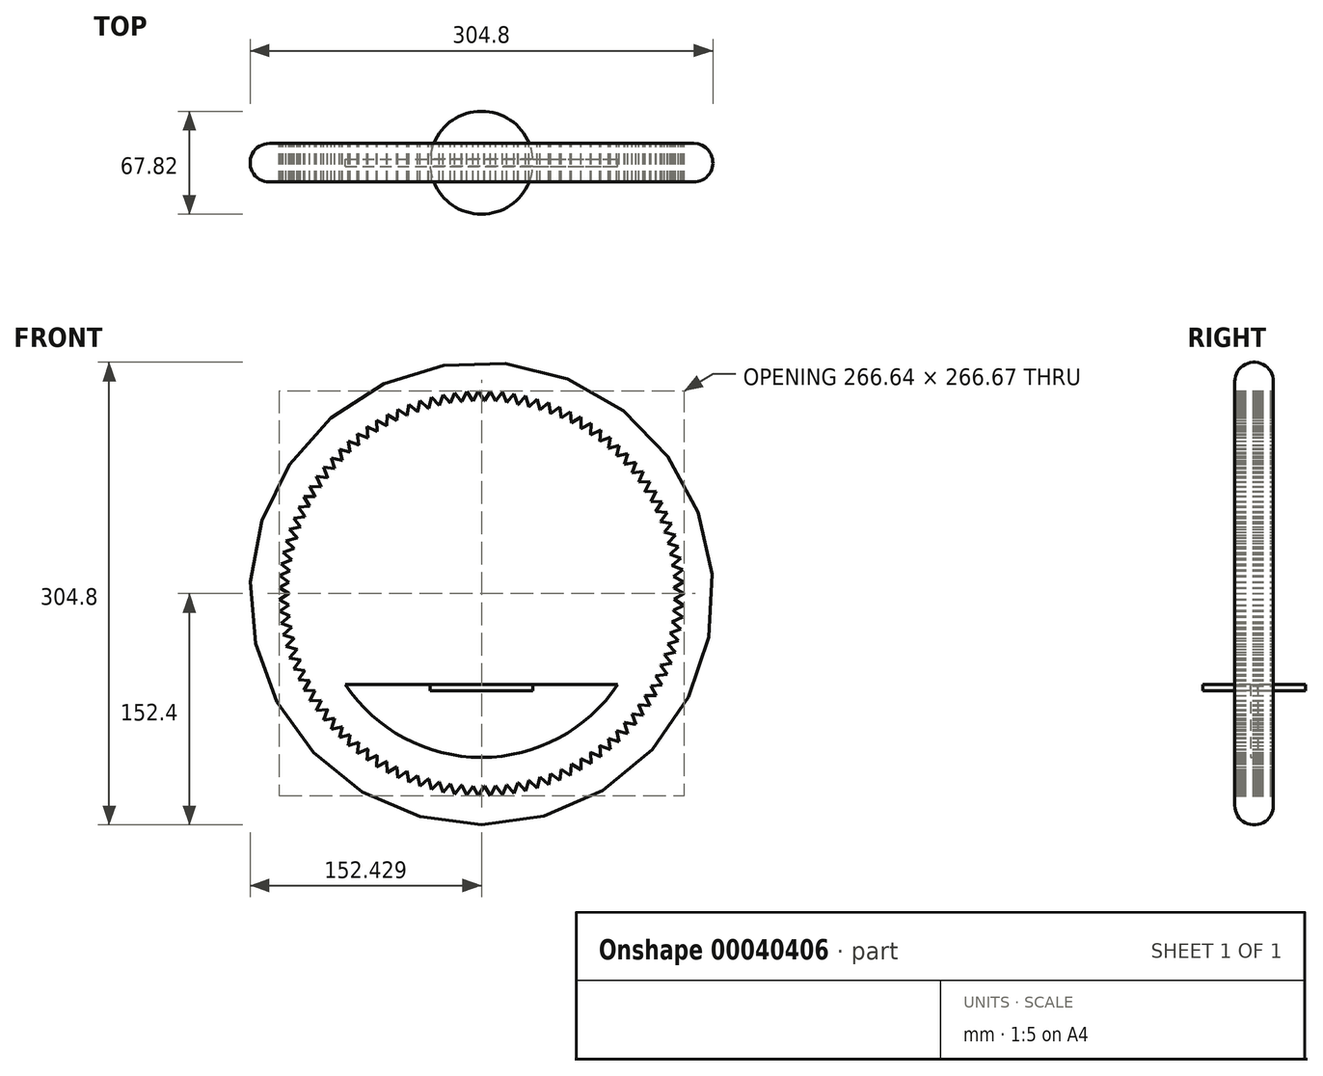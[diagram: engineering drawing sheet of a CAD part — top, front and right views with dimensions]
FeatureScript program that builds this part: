
annotation { "Feature Type Name" : "Feature", "Feature Type Description" : "" }
export const myFeature = defineFeature(function(context is Context, id is Id, definition is map)
    precondition{}
    {
        {
            var Q0;
            Q0=qCreatedBy(makeId("Front.planeOp"),FACE);
            var sketch = newSketch(context, id + "F0", { "sketchPlane" : qUnion([Q0])});
            skCircle(sketch, "E0", {"center": v(0, 0) * mm, "radius": 152.4 * mm});
            skCircle(sketch, "E1", {"center": v(0, 0) * mm, "radius": 127 * mm});
            skCircle(sketch, "E2", {"center": v(0, 0) * mm, "radius": 133.35 * mm, "construction": true});
            skLineSegment(sketch, "E3", {"start": v(133.35, 0) * mm, "end": v(126.95, 3.7) * mm});
            skLineSegment(sketch, "E4", {"start": v(133.35, 0) * mm, "end": v(126.95, -3.7) * mm});
            skLineSegment(sketch, "E5", {"start": v(0, 0) * mm, "end": v(133.35, 0) * mm, "construction": true});
            skLineSegment(sketch, "E6.1.0", {"start": v(133.12, 7.83) * mm, "end": v(126.94, 3.76) * mm});
            skLineSegment(sketch, "E6.1.1", {"start": v(133.12, 7.83) * mm, "end": v(126.51, 11.14) * mm});
            skLineSegment(sketch, "E6.2.0", {"start": v(132.43, 15.63) * mm, "end": v(126.5, 11.2) * mm});
            skLineSegment(sketch, "E6.2.1", {"start": v(132.43, 15.63) * mm, "end": v(125.64, 18.55) * mm});
            skLineSegment(sketch, "E6.3.0", {"start": v(131.29, 23.37) * mm, "end": v(125.63, 18.6) * mm});
            skLineSegment(sketch, "E6.3.1", {"start": v(131.29, 23.37) * mm, "end": v(124.33, 25.89) * mm});
            skLineSegment(sketch, "E6.4.0", {"start": v(129.69, 31.03) * mm, "end": v(124.32, 25.95) * mm});
            skLineSegment(sketch, "E6.4.1", {"start": v(129.69, 31.03) * mm, "end": v(122.6, 33.14) * mm});
            skLineSegment(sketch, "E6.5.0", {"start": v(127.64, 38.6) * mm, "end": v(122.58, 33.2) * mm});
            skLineSegment(sketch, "E6.5.1", {"start": v(127.64, 38.6) * mm, "end": v(120.44, 40.28) * mm});
            skLineSegment(sketch, "E6.6.0", {"start": v(125.16, 46.02) * mm, "end": v(120.42, 40.34) * mm});
            skLineSegment(sketch, "E6.6.1", {"start": v(125.16, 46.02) * mm, "end": v(117.87, 47.28) * mm});
            skLineSegment(sketch, "E6.7.0", {"start": v(122.24, 53.28) * mm, "end": v(117.85, 47.33) * mm});
            skLineSegment(sketch, "E6.7.1", {"start": v(122.24, 53.28) * mm, "end": v(114.9, 54.11) * mm});
            skLineSegment(sketch, "E6.8.0", {"start": v(118.9, 60.37) * mm, "end": v(114.87, 54.17) * mm});
            skLineSegment(sketch, "E6.8.1", {"start": v(118.9, 60.37) * mm, "end": v(111.52, 60.76) * mm});
            skLineSegment(sketch, "E6.9.0", {"start": v(115.16, 67.24) * mm, "end": v(111.5, 60.82) * mm});
            skLineSegment(sketch, "E6.9.1", {"start": v(115.16, 67.24) * mm, "end": v(107.76, 67.2) * mm});
            skLineSegment(sketch, "E6.10.0", {"start": v(111.01, 73.88) * mm, "end": v(107.73, 67.26) * mm});
            skLineSegment(sketch, "E6.10.1", {"start": v(111.01, 73.88) * mm, "end": v(103.63, 73.41) * mm});
            skLineSegment(sketch, "E6.11.0", {"start": v(106.48, 80.27) * mm, "end": v(103.6, 73.46) * mm});
            skLineSegment(sketch, "E6.11.1", {"start": v(106.48, 80.27) * mm, "end": v(99.15, 79.37) * mm});
            skLineSegment(sketch, "E6.12.0", {"start": v(101.6, 86.38) * mm, "end": v(99.1, 79.42) * mm});
            skLineSegment(sketch, "E6.12.1", {"start": v(101.6, 86.38) * mm, "end": v(94.32, 85.05) * mm});
            skLineSegment(sketch, "E6.13.0", {"start": v(96.35, 92.2) * mm, "end": v(94.28, 85.1) * mm});
            skLineSegment(sketch, "E6.13.1", {"start": v(96.35, 92.2) * mm, "end": v(89.16, 90.44) * mm});
            skLineSegment(sketch, "E6.14.0", {"start": v(90.77, 97.69) * mm, "end": v(89.12, 90.48) * mm});
            skLineSegment(sketch, "E6.14.1", {"start": v(90.77, 97.69) * mm, "end": v(83.7, 95.51) * mm});
            skLineSegment(sketch, "E6.15.0", {"start": v(84.88, 102.85) * mm, "end": v(83.66, 95.56) * mm});
            skLineSegment(sketch, "E6.15.1", {"start": v(84.88, 102.85) * mm, "end": v(77.95, 100.26) * mm});
            skLineSegment(sketch, "E6.16.0", {"start": v(78.7, 107.65) * mm, "end": v(77.9, 100.3) * mm});
            skLineSegment(sketch, "E6.16.1", {"start": v(78.7, 107.65) * mm, "end": v(71.93, 104.66) * mm});
            skLineSegment(sketch, "E6.17.0", {"start": v(72.24, 112.08) * mm, "end": v(71.88, 104.7) * mm});
            skLineSegment(sketch, "E6.17.1", {"start": v(72.24, 112.08) * mm, "end": v(65.67, 108.7) * mm});
            skLineSegment(sketch, "E6.18.0", {"start": v(65.54, 116.13) * mm, "end": v(65.61, 108.74) * mm});
            skLineSegment(sketch, "E6.18.1", {"start": v(65.54, 116.13) * mm, "end": v(59.17, 112.37) * mm});
            skLineSegment(sketch, "E6.19.0", {"start": v(58.61, 119.78) * mm, "end": v(59.12, 112.4) * mm});
            skLineSegment(sketch, "E6.19.1", {"start": v(58.61, 119.78) * mm, "end": v(52.48, 115.65) * mm});
            skLineSegment(sketch, "E6.20.0", {"start": v(51.48, 123.01) * mm, "end": v(52.42, 115.68) * mm});
            skLineSegment(sketch, "E6.20.1", {"start": v(51.48, 123.01) * mm, "end": v(45.6, 118.53) * mm});
            skLineSegment(sketch, "E6.21.0", {"start": v(44.17, 125.82) * mm, "end": v(45.54, 118.55) * mm});
            skLineSegment(sketch, "E6.21.1", {"start": v(44.17, 125.82) * mm, "end": v(38.56, 121) * mm});
            skLineSegment(sketch, "E6.22.0", {"start": v(36.71, 128.2) * mm, "end": v(38.5, 121.02) * mm});
            skLineSegment(sketch, "E6.22.1", {"start": v(36.71, 128.2) * mm, "end": v(31.4, 123.06) * mm});
            skLineSegment(sketch, "E6.23.0", {"start": v(29.13, 130.13) * mm, "end": v(31.34, 123.07) * mm});
            skLineSegment(sketch, "E6.23.1", {"start": v(29.13, 130.13) * mm, "end": v(24.12, 124.69) * mm});
            skLineSegment(sketch, "E6.24.0", {"start": v(21.44, 131.62) * mm, "end": v(24.06, 124.7) * mm});
            skLineSegment(sketch, "E6.24.1", {"start": v(21.44, 131.62) * mm, "end": v(16.76, 125.89) * mm});
            skLineSegment(sketch, "E6.25.0", {"start": v(13.68, 132.65) * mm, "end": v(16.7, 125.9) * mm});
            skLineSegment(sketch, "E6.25.1", {"start": v(13.68, 132.65) * mm, "end": v(9.34, 126.66) * mm});
            skLineSegment(sketch, "E6.26.0", {"start": v(5.87, 133.22) * mm, "end": v(9.28, 126.66) * mm});
            skLineSegment(sketch, "E6.26.1", {"start": v(5.87, 133.22) * mm, "end": v(1.9, 126.99) * mm});
            skLineSegment(sketch, "E6.27.0", {"start": v(-1.96, 133.34) * mm, "end": v(1.83, 126.99) * mm});
            skLineSegment(sketch, "E6.27.1", {"start": v(-1.96, 133.34) * mm, "end": v(-5.56, 126.88) * mm});
            skLineSegment(sketch, "E6.28.0", {"start": v(-9.78, 133) * mm, "end": v(-5.62, 126.88) * mm});
            skLineSegment(sketch, "E6.28.1", {"start": v(-9.78, 133) * mm, "end": v(-13, 126.33) * mm});
            skLineSegment(sketch, "E6.29.0", {"start": v(-17.57, 132.19) * mm, "end": v(-13.06, 126.33) * mm});
            skLineSegment(sketch, "E6.29.1", {"start": v(-17.57, 132.19) * mm, "end": v(-20.39, 125.35) * mm});
            skLineSegment(sketch, "E6.30.0", {"start": v(-25.3, 130.93) * mm, "end": v(-20.45, 125.34) * mm});
            skLineSegment(sketch, "E6.30.1", {"start": v(-25.3, 130.93) * mm, "end": v(-27.71, 123.94) * mm});
            skLineSegment(sketch, "E6.31.0", {"start": v(-32.94, 129.22) * mm, "end": v(-27.77, 123.93) * mm});
            skLineSegment(sketch, "E6.31.1", {"start": v(-32.94, 129.22) * mm, "end": v(-34.94, 122.1) * mm});
            skLineSegment(sketch, "E6.32.0", {"start": v(-40.46, 127.06) * mm, "end": v(-35, 122.08) * mm});
            skLineSegment(sketch, "E6.32.1", {"start": v(-40.46, 127.06) * mm, "end": v(-42.04, 119.84) * mm});
            skLineSegment(sketch, "E6.33.0", {"start": v(-47.85, 124.47) * mm, "end": v(-42.1, 119.82) * mm});
            skLineSegment(sketch, "E6.33.1", {"start": v(-47.85, 124.47) * mm, "end": v(-49, 117.17) * mm});
            skLineSegment(sketch, "E6.34.0", {"start": v(-55.07, 121.45) * mm, "end": v(-49.06, 117.14) * mm});
            skLineSegment(sketch, "E6.34.1", {"start": v(-55.07, 121.45) * mm, "end": v(-55.8, 114.09) * mm});
            skLineSegment(sketch, "E6.35.0", {"start": v(-62.1, 118) * mm, "end": v(-55.85, 114.06) * mm});
            skLineSegment(sketch, "E6.35.1", {"start": v(-62.1, 118) * mm, "end": v(-62.4, 110.62) * mm});
            skLineSegment(sketch, "E6.36.0", {"start": v(-68.92, 114.16) * mm, "end": v(-62.45, 110.59) * mm});
            skLineSegment(sketch, "E6.36.1", {"start": v(-68.92, 114.16) * mm, "end": v(-68.78, 106.76) * mm});
            skLineSegment(sketch, "E6.37.0", {"start": v(-75.5, 109.92) * mm, "end": v(-68.83, 106.73) * mm});
            skLineSegment(sketch, "E6.37.1", {"start": v(-75.5, 109.92) * mm, "end": v(-74.93, 102.54) * mm});
            skLineSegment(sketch, "E6.38.0", {"start": v(-81.82, 105.3) * mm, "end": v(-74.98, 102.5) * mm});
            skLineSegment(sketch, "E6.38.1", {"start": v(-81.82, 105.3) * mm, "end": v(-80.81, 97.97) * mm});
            skLineSegment(sketch, "E6.39.0", {"start": v(-87.86, 100.31) * mm, "end": v(-80.86, 97.93) * mm});
            skLineSegment(sketch, "E6.39.1", {"start": v(-87.86, 100.31) * mm, "end": v(-86.42, 93.06) * mm});
            skLineSegment(sketch, "E6.40.0", {"start": v(-93.6, 94.98) * mm, "end": v(-86.47, 93.02) * mm});
            skLineSegment(sketch, "E6.40.1", {"start": v(-93.6, 94.98) * mm, "end": v(-91.74, 87.83) * mm});
            skLineSegment(sketch, "E6.41.0", {"start": v(-99.01, 89.33) * mm, "end": v(-91.78, 87.78) * mm});
            skLineSegment(sketch, "E6.41.1", {"start": v(-99.01, 89.33) * mm, "end": v(-96.73, 82.3) * mm});
            skLineSegment(sketch, "E6.42.0", {"start": v(-104.08, 83.36) * mm, "end": v(-96.77, 82.24) * mm});
            skLineSegment(sketch, "E6.42.1", {"start": v(-104.08, 83.36) * mm, "end": v(-101.4, 76.47) * mm});
            skLineSegment(sketch, "E6.43.0", {"start": v(-108.8, 77.1) * mm, "end": v(-101.43, 76.42) * mm});
            skLineSegment(sketch, "E6.43.1", {"start": v(-108.8, 77.1) * mm, "end": v(-105.7, 70.39) * mm});
            skLineSegment(sketch, "E6.44.0", {"start": v(-113.13, 70.6) * mm, "end": v(-105.74, 70.34) * mm});
            skLineSegment(sketch, "E6.44.1", {"start": v(-113.13, 70.6) * mm, "end": v(-109.66, 64.06) * mm});
            skLineSegment(sketch, "E6.45.0", {"start": v(-117.08, 63.83) * mm, "end": v(-109.69, 64.01) * mm});
            skLineSegment(sketch, "E6.45.1", {"start": v(-117.08, 63.83) * mm, "end": v(-113.23, 57.52) * mm});
            skLineSegment(sketch, "E6.46.0", {"start": v(-120.63, 56.85) * mm, "end": v(-113.26, 57.46) * mm});
            skLineSegment(sketch, "E6.46.1", {"start": v(-120.63, 56.85) * mm, "end": v(-116.4, 50.77) * mm});
            skLineSegment(sketch, "E6.47.0", {"start": v(-123.75, 49.67) * mm, "end": v(-116.43, 50.72) * mm});
            skLineSegment(sketch, "E6.47.1", {"start": v(-123.75, 49.67) * mm, "end": v(-119.19, 43.85) * mm});
            skLineSegment(sketch, "E6.48.0", {"start": v(-126.46, 42.32) * mm, "end": v(-119.2, 43.8) * mm});
            skLineSegment(sketch, "E6.48.1", {"start": v(-126.46, 42.32) * mm, "end": v(-121.56, 36.78) * mm});
            skLineSegment(sketch, "E6.49.0", {"start": v(-128.72, 34.83) * mm, "end": v(-121.57, 36.72) * mm});
            skLineSegment(sketch, "E6.49.1", {"start": v(-128.72, 34.83) * mm, "end": v(-123.5, 29.59) * mm});
            skLineSegment(sketch, "E6.50.0", {"start": v(-130.54, 27.21) * mm, "end": v(-123.52, 29.53) * mm});
            skLineSegment(sketch, "E6.50.1", {"start": v(-130.54, 27.21) * mm, "end": v(-125.03, 22.29) * mm});
            skLineSegment(sketch, "E6.51.0", {"start": v(-131.92, 19.5) * mm, "end": v(-125.04, 22.23) * mm});
            skLineSegment(sketch, "E6.51.1", {"start": v(-131.92, 19.5) * mm, "end": v(-126.12, 14.91) * mm});
            skLineSegment(sketch, "E6.52.0", {"start": v(-132.83, 11.73) * mm, "end": v(-126.13, 14.85) * mm});
            skLineSegment(sketch, "E6.52.1", {"start": v(-132.83, 11.73) * mm, "end": v(-126.78, 7.48) * mm});
            skLineSegment(sketch, "E6.53.0", {"start": v(-133.3, 3.91) * mm, "end": v(-126.78, 7.42) * mm});
            skLineSegment(sketch, "E6.53.1", {"start": v(-133.3, 3.91) * mm, "end": v(-127, 0.03) * mm});
            skLineSegment(sketch, "E6.54.0", {"start": v(-133.3, -3.91) * mm, "end": v(-127, -0.03) * mm});
            skLineSegment(sketch, "E6.54.1", {"start": v(-133.3, -3.91) * mm, "end": v(-126.78, -7.42) * mm});
            skLineSegment(sketch, "E6.55.0", {"start": v(-132.83, -11.73) * mm, "end": v(-126.78, -7.48) * mm});
            skLineSegment(sketch, "E6.55.1", {"start": v(-132.83, -11.73) * mm, "end": v(-126.13, -14.85) * mm});
            skLineSegment(sketch, "E6.56.0", {"start": v(-131.92, -19.5) * mm, "end": v(-126.12, -14.91) * mm});
            skLineSegment(sketch, "E6.56.1", {"start": v(-131.92, -19.5) * mm, "end": v(-125.04, -22.23) * mm});
            skLineSegment(sketch, "E6.57.0", {"start": v(-130.54, -27.21) * mm, "end": v(-125.03, -22.29) * mm});
            skLineSegment(sketch, "E6.57.1", {"start": v(-130.54, -27.21) * mm, "end": v(-123.52, -29.53) * mm});
            skLineSegment(sketch, "E6.58.0", {"start": v(-128.72, -34.83) * mm, "end": v(-123.5, -29.59) * mm});
            skLineSegment(sketch, "E6.58.1", {"start": v(-128.72, -34.83) * mm, "end": v(-121.57, -36.72) * mm});
            skLineSegment(sketch, "E6.59.0", {"start": v(-126.46, -42.32) * mm, "end": v(-121.56, -36.78) * mm});
            skLineSegment(sketch, "E6.59.1", {"start": v(-126.46, -42.32) * mm, "end": v(-119.2, -43.8) * mm});
            skLineSegment(sketch, "E6.60.0", {"start": v(-123.75, -49.67) * mm, "end": v(-119.19, -43.85) * mm});
            skLineSegment(sketch, "E6.60.1", {"start": v(-123.75, -49.67) * mm, "end": v(-116.43, -50.72) * mm});
            skLineSegment(sketch, "E6.61.0", {"start": v(-120.63, -56.85) * mm, "end": v(-116.4, -50.77) * mm});
            skLineSegment(sketch, "E6.61.1", {"start": v(-120.63, -56.85) * mm, "end": v(-113.26, -57.46) * mm});
            skLineSegment(sketch, "E6.62.0", {"start": v(-117.08, -63.83) * mm, "end": v(-113.23, -57.52) * mm});
            skLineSegment(sketch, "E6.62.1", {"start": v(-117.08, -63.83) * mm, "end": v(-109.69, -64.01) * mm});
            skLineSegment(sketch, "E6.63.0", {"start": v(-113.13, -70.6) * mm, "end": v(-109.66, -64.06) * mm});
            skLineSegment(sketch, "E6.63.1", {"start": v(-113.13, -70.6) * mm, "end": v(-105.74, -70.34) * mm});
            skLineSegment(sketch, "E6.64.0", {"start": v(-108.8, -77.1) * mm, "end": v(-105.7, -70.39) * mm});
            skLineSegment(sketch, "E6.64.1", {"start": v(-108.8, -77.1) * mm, "end": v(-101.43, -76.42) * mm});
            skLineSegment(sketch, "E6.65.0", {"start": v(-104.08, -83.36) * mm, "end": v(-101.4, -76.47) * mm});
            skLineSegment(sketch, "E6.65.1", {"start": v(-104.08, -83.36) * mm, "end": v(-96.77, -82.24) * mm});
            skLineSegment(sketch, "E6.66.0", {"start": v(-99.01, -89.33) * mm, "end": v(-96.73, -82.3) * mm});
            skLineSegment(sketch, "E6.66.1", {"start": v(-99.01, -89.33) * mm, "end": v(-91.78, -87.78) * mm});
            skLineSegment(sketch, "E6.67.0", {"start": v(-93.6, -94.98) * mm, "end": v(-91.74, -87.83) * mm});
            skLineSegment(sketch, "E6.67.1", {"start": v(-93.6, -94.98) * mm, "end": v(-86.47, -93.02) * mm});
            skLineSegment(sketch, "E6.68.0", {"start": v(-87.86, -100.31) * mm, "end": v(-86.42, -93.06) * mm});
            skLineSegment(sketch, "E6.68.1", {"start": v(-87.86, -100.31) * mm, "end": v(-80.86, -97.93) * mm});
            skLineSegment(sketch, "E6.69.0", {"start": v(-81.82, -105.3) * mm, "end": v(-80.81, -97.97) * mm});
            skLineSegment(sketch, "E6.69.1", {"start": v(-81.82, -105.3) * mm, "end": v(-74.98, -102.5) * mm});
            skLineSegment(sketch, "E6.70.0", {"start": v(-75.5, -109.92) * mm, "end": v(-74.93, -102.54) * mm});
            skLineSegment(sketch, "E6.70.1", {"start": v(-75.5, -109.92) * mm, "end": v(-68.83, -106.73) * mm});
            skLineSegment(sketch, "E6.71.0", {"start": v(-68.92, -114.16) * mm, "end": v(-68.78, -106.76) * mm});
            skLineSegment(sketch, "E6.71.1", {"start": v(-68.92, -114.16) * mm, "end": v(-62.45, -110.59) * mm});
            skLineSegment(sketch, "E6.72.0", {"start": v(-62.1, -118) * mm, "end": v(-62.4, -110.62) * mm});
            skLineSegment(sketch, "E6.72.1", {"start": v(-62.1, -118) * mm, "end": v(-55.85, -114.06) * mm});
            skLineSegment(sketch, "E6.73.0", {"start": v(-55.07, -121.45) * mm, "end": v(-55.8, -114.09) * mm});
            skLineSegment(sketch, "E6.73.1", {"start": v(-55.07, -121.45) * mm, "end": v(-49.06, -117.14) * mm});
            skLineSegment(sketch, "E6.74.0", {"start": v(-47.85, -124.47) * mm, "end": v(-49, -117.17) * mm});
            skLineSegment(sketch, "E6.74.1", {"start": v(-47.85, -124.47) * mm, "end": v(-42.1, -119.82) * mm});
            skLineSegment(sketch, "E6.75.0", {"start": v(-40.46, -127.06) * mm, "end": v(-42.04, -119.84) * mm});
            skLineSegment(sketch, "E6.75.1", {"start": v(-40.46, -127.06) * mm, "end": v(-35, -122.08) * mm});
            skLineSegment(sketch, "E6.76.0", {"start": v(-32.94, -129.22) * mm, "end": v(-34.94, -122.1) * mm});
            skLineSegment(sketch, "E6.76.1", {"start": v(-32.94, -129.22) * mm, "end": v(-27.77, -123.93) * mm});
            skLineSegment(sketch, "E6.77.0", {"start": v(-25.3, -130.93) * mm, "end": v(-27.71, -123.94) * mm});
            skLineSegment(sketch, "E6.77.1", {"start": v(-25.3, -130.93) * mm, "end": v(-20.45, -125.34) * mm});
            skLineSegment(sketch, "E6.78.0", {"start": v(-17.57, -132.19) * mm, "end": v(-20.39, -125.35) * mm});
            skLineSegment(sketch, "E6.78.1", {"start": v(-17.57, -132.19) * mm, "end": v(-13.06, -126.33) * mm});
            skLineSegment(sketch, "E6.79.0", {"start": v(-9.78, -133) * mm, "end": v(-13, -126.33) * mm});
            skLineSegment(sketch, "E6.79.1", {"start": v(-9.78, -133) * mm, "end": v(-5.62, -126.88) * mm});
            skLineSegment(sketch, "E6.80.0", {"start": v(-1.96, -133.34) * mm, "end": v(-5.56, -126.88) * mm});
            skLineSegment(sketch, "E6.80.1", {"start": v(-1.96, -133.34) * mm, "end": v(1.83, -126.99) * mm});
            skLineSegment(sketch, "E6.81.0", {"start": v(5.87, -133.22) * mm, "end": v(1.9, -126.99) * mm});
            skLineSegment(sketch, "E6.81.1", {"start": v(5.87, -133.22) * mm, "end": v(9.28, -126.66) * mm});
            skLineSegment(sketch, "E6.82.0", {"start": v(13.68, -132.65) * mm, "end": v(9.34, -126.66) * mm});
            skLineSegment(sketch, "E6.82.1", {"start": v(13.68, -132.65) * mm, "end": v(16.7, -125.9) * mm});
            skLineSegment(sketch, "E6.83.0", {"start": v(21.44, -131.62) * mm, "end": v(16.76, -125.89) * mm});
            skLineSegment(sketch, "E6.83.1", {"start": v(21.44, -131.62) * mm, "end": v(24.06, -124.7) * mm});
            skLineSegment(sketch, "E6.84.0", {"start": v(29.13, -130.13) * mm, "end": v(24.12, -124.69) * mm});
            skLineSegment(sketch, "E6.84.1", {"start": v(29.13, -130.13) * mm, "end": v(31.34, -123.07) * mm});
            skLineSegment(sketch, "E6.85.0", {"start": v(36.71, -128.2) * mm, "end": v(31.4, -123.06) * mm});
            skLineSegment(sketch, "E6.85.1", {"start": v(36.71, -128.2) * mm, "end": v(38.5, -121.02) * mm});
            skLineSegment(sketch, "E6.86.0", {"start": v(44.17, -125.82) * mm, "end": v(38.56, -121) * mm});
            skLineSegment(sketch, "E6.86.1", {"start": v(44.17, -125.82) * mm, "end": v(45.54, -118.55) * mm});
            skLineSegment(sketch, "E6.87.0", {"start": v(51.48, -123.01) * mm, "end": v(45.6, -118.53) * mm});
            skLineSegment(sketch, "E6.87.1", {"start": v(51.48, -123.01) * mm, "end": v(52.42, -115.68) * mm});
            skLineSegment(sketch, "E6.88.0", {"start": v(58.61, -119.78) * mm, "end": v(52.48, -115.65) * mm});
            skLineSegment(sketch, "E6.88.1", {"start": v(58.61, -119.78) * mm, "end": v(59.12, -112.4) * mm});
            skLineSegment(sketch, "E6.89.0", {"start": v(65.54, -116.13) * mm, "end": v(59.17, -112.37) * mm});
            skLineSegment(sketch, "E6.89.1", {"start": v(65.54, -116.13) * mm, "end": v(65.61, -108.74) * mm});
            skLineSegment(sketch, "E6.90.0", {"start": v(72.24, -112.08) * mm, "end": v(65.67, -108.7) * mm});
            skLineSegment(sketch, "E6.90.1", {"start": v(72.24, -112.08) * mm, "end": v(71.88, -104.7) * mm});
            skLineSegment(sketch, "E6.91.0", {"start": v(78.7, -107.65) * mm, "end": v(71.93, -104.66) * mm});
            skLineSegment(sketch, "E6.91.1", {"start": v(78.7, -107.65) * mm, "end": v(77.9, -100.3) * mm});
            skLineSegment(sketch, "E6.92.0", {"start": v(84.88, -102.85) * mm, "end": v(77.95, -100.26) * mm});
            skLineSegment(sketch, "E6.92.1", {"start": v(84.88, -102.85) * mm, "end": v(83.66, -95.56) * mm});
            skLineSegment(sketch, "E6.93.0", {"start": v(90.77, -97.69) * mm, "end": v(83.7, -95.51) * mm});
            skLineSegment(sketch, "E6.93.1", {"start": v(90.77, -97.69) * mm, "end": v(89.12, -90.48) * mm});
            skLineSegment(sketch, "E6.94.0", {"start": v(96.35, -92.2) * mm, "end": v(89.16, -90.44) * mm});
            skLineSegment(sketch, "E6.94.1", {"start": v(96.35, -92.2) * mm, "end": v(94.28, -85.1) * mm});
            skLineSegment(sketch, "E6.95.0", {"start": v(101.6, -86.38) * mm, "end": v(94.32, -85.05) * mm});
            skLineSegment(sketch, "E6.95.1", {"start": v(101.6, -86.38) * mm, "end": v(99.1, -79.42) * mm});
            skLineSegment(sketch, "E6.96.0", {"start": v(106.48, -80.27) * mm, "end": v(99.15, -79.37) * mm});
            skLineSegment(sketch, "E6.96.1", {"start": v(106.48, -80.27) * mm, "end": v(103.6, -73.46) * mm});
            skLineSegment(sketch, "E6.97.0", {"start": v(111.01, -73.88) * mm, "end": v(103.63, -73.41) * mm});
            skLineSegment(sketch, "E6.97.1", {"start": v(111.01, -73.88) * mm, "end": v(107.73, -67.26) * mm});
            skLineSegment(sketch, "E6.98.0", {"start": v(115.16, -67.24) * mm, "end": v(107.76, -67.2) * mm});
            skLineSegment(sketch, "E6.98.1", {"start": v(115.16, -67.24) * mm, "end": v(111.5, -60.82) * mm});
            skLineSegment(sketch, "E6.99.0", {"start": v(118.9, -60.37) * mm, "end": v(111.52, -60.76) * mm});
            skLineSegment(sketch, "E6.99.1", {"start": v(118.9, -60.37) * mm, "end": v(114.87, -54.17) * mm});
            skLineSegment(sketch, "E7.3.100.0", {"start": v(122.24, -53.28) * mm, "end": v(117.85, -47.33) * mm});
            skLineSegment(sketch, "E7.5.100.0", {"start": v(122.24, -53.28) * mm, "end": v(114.9, -54.11) * mm});
            skLineSegment(sketch, "E7.3.101.0", {"start": v(125.16, -46.02) * mm, "end": v(120.42, -40.34) * mm});
            skLineSegment(sketch, "E7.5.101.0", {"start": v(125.16, -46.02) * mm, "end": v(117.87, -47.28) * mm});
            skLineSegment(sketch, "E7.3.102.0", {"start": v(127.64, -38.6) * mm, "end": v(122.58, -33.2) * mm});
            skLineSegment(sketch, "E7.5.102.0", {"start": v(127.64, -38.6) * mm, "end": v(120.44, -40.28) * mm});
            skLineSegment(sketch, "E7.3.103.0", {"start": v(129.69, -31.03) * mm, "end": v(124.32, -25.95) * mm});
            skLineSegment(sketch, "E7.5.103.0", {"start": v(129.69, -31.03) * mm, "end": v(122.6, -33.14) * mm});
            skLineSegment(sketch, "E7.3.104.0", {"start": v(131.29, -23.37) * mm, "end": v(125.63, -18.6) * mm});
            skLineSegment(sketch, "E7.5.104.0", {"start": v(131.29, -23.37) * mm, "end": v(124.33, -25.89) * mm});
            skLineSegment(sketch, "E8.3.105.0", {"start": v(132.43, -15.63) * mm, "end": v(126.5, -11.2) * mm});
            skLineSegment(sketch, "E8.5.105.0", {"start": v(132.43, -15.63) * mm, "end": v(125.64, -18.55) * mm});
            skLineSegment(sketch, "E8.3.106.0", {"start": v(133.12, -7.83) * mm, "end": v(126.94, -3.76) * mm});
            skLineSegment(sketch, "E8.5.106.0", {"start": v(133.12, -7.83) * mm, "end": v(126.51, -11.14) * mm});
            skSolve(sketch);
        }
        {
            var Q0;
            Q0=makeQuery(id+"F0.imprint","IMPRINT",FACE,{"disambiguationData":[TD([[makeQuery(id+"F0.imprint","IMPRINT",EDGE,{"derivedFrom":sQuery(id+"F0.wireOp",EDGE,"E0")}),1.0]])]});
            extrude(context, id + "F1", {"entities" : qUnion([Q0]), "depth" : 12.7 * mm, "hasSecondDirection" : true, "secondDirectionOppositeDirection" : true, "secondDirectionDepth" : 12.7 * mm});
        }
        {
            var Q0;
            Q0=makeQuery(id+"F1.opExtrude","SWEPT_FACE",FACE,{"disambiguationData":[OSD([sQuery(id+"F0.wireOp",EDGE,"E0")])]});
            var Q1;
            Q1=makeQuery(id+"F1.opExtrude","CAP_EDGE",EDGE,{"disambiguationData":[OSD([sQuery(id+"F0.wireOp",EDGE,"E0")])],"isStart":true});
            fillet(context, id + "F2", {"entities" : qUnion([Q0, Q1]), "radius" : 12.7 * mm, "tangentPropagation" : true, "allowEdgeOverflow" : false});
        }
        {
            var Q0;
            Q0=qCreatedBy(makeId("Front.planeOp"),FACE);
            var sketch = newSketch(context, id + "F3", { "sketchPlane" : qUnion([Q0])});
            skLineSegment(sketch, "E9", {"start": v(-89.71, -60) * mm, "end": v(89.71, -60) * mm});
            skArc(sketch, "E10", {"start": v(-89.71, -60) * mm, "mid": v(0, -107.93) * mm, "end": v(89.71, -60) * mm});
            skSolve(sketch);
        }
        {
            var Q0;
            Q0=makeQuery(id+"F3.imprint","IMPRINT",FACE,{"disambiguationData":[TD([[makeQuery(id+"F3.imprint","IMPRINT",EDGE,{"derivedFrom":sQuery(id+"F3.wireOp",EDGE,"E9")}),-1.0]])]});
            extrude(context, id + "F4", {"entities" : qUnion([Q0]), "endBound" : BoundingType.SYMMETRIC, "depth" : 5 * mm});
        }
        {
            var Q0;
            Q0=makeQuery(id+"F4.opExtrude","SWEPT_FACE",FACE,{"disambiguationData":[OSD([sQuery(id+"F3.wireOp",EDGE,"E9")])]});
            var sketch = newSketch(context, id + "F5", { "sketchPlane" : qUnion([Q0])});
            skCircle(sketch, "E11", {"center": v(0, 0) * mm, "radius": 33.91 * mm});
            skSolve(sketch);
        }
        {
            var Q0;
            {var subQ0=makeQuery(id+"F4.opExtrude","CAP_EDGE",EDGE,{"disambiguationData":[OSD([sQuery(id+"F3.wireOp",EDGE,"E9")])],"isStart":true});var subQ1=sQuery(id+"F5.wireOp",EDGE,"E11");var subQ3=makeQuery(id+"F5.imprint","INTERSECT",VERTEX,{"disambiguationData":[OD(0.0)],"derivedFrom":[subQ0,subQ1]});Q0=makeQuery(id+"F5.imprint","IMPRINT",FACE,{"disambiguationData":[TD([[makeQuery(id+"F5.imprint","IMPRINT",EDGE,{"disambiguationData":[TD([[subQ3,1.0]])],"derivedFrom":subQ1}),1.0]])]});}
            var Q1;
            {var subQ0=sQuery(id+"F3.wireOp",EDGE,"E9");var subQ2=sQuery(id+"F5.wireOp",EDGE,"E11");var subQ5=makeQuery(id+"F4.opExtrude","CAP_EDGE",EDGE,{"disambiguationData":[OSD([subQ0])],"isStart":true});var subQ7=makeQuery(id+"F5.imprint","INTERSECT",VERTEX,{"disambiguationData":[OD(0.0)],"derivedFrom":[subQ5,subQ2]});Q1=makeQuery(id+"F5.imprint","IMPRINT",FACE,{"disambiguationData":[TD([[makeQuery(id+"F5.imprint","IMPRINT",EDGE,{"disambiguationData":[TD([[subQ7,-1.0]])],"derivedFrom":subQ2}),1.0]])]});}
            var Q2;
            {var subQ0=makeQuery(id+"F4.opExtrude","CAP_EDGE",EDGE,{"disambiguationData":[OSD([sQuery(id+"F3.wireOp",EDGE,"E9")])],"isStart":false});var subQ1=sQuery(id+"F5.wireOp",EDGE,"E11");var subQ3=makeQuery(id+"F5.imprint","INTERSECT",VERTEX,{"disambiguationData":[OD(0.0)],"derivedFrom":[subQ0,subQ1]});Q2=makeQuery(id+"F5.imprint","IMPRINT",FACE,{"disambiguationData":[TD([[makeQuery(id+"F5.imprint","IMPRINT",EDGE,{"disambiguationData":[TD([[subQ3,-1.0]])],"derivedFrom":subQ1}),1.0]])]});}
            extrude(context, id + "F6", {"entities" : qUnion([Q0, Q1, Q2]), "operationType" : NewBodyOperationType.ADD, "oppositeDirection" : true, "depth" : 4 * mm});
        }
    });
